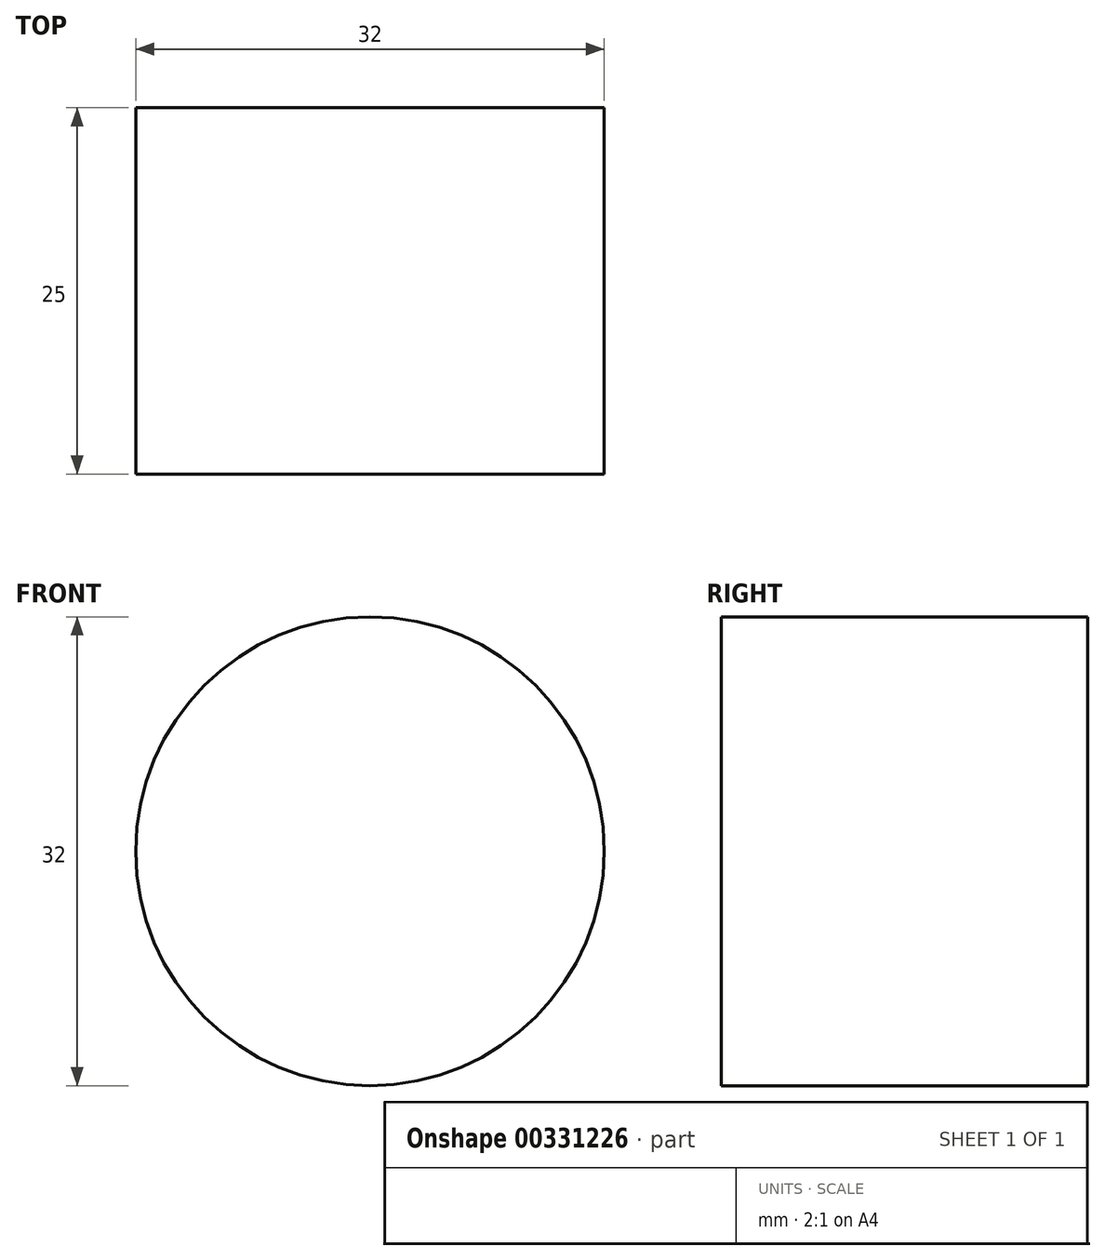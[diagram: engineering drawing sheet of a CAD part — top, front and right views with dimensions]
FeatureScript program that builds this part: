
annotation { "Feature Type Name" : "Feature", "Feature Type Description" : "" }
export const myFeature = defineFeature(function(context is Context, id is Id, definition is map)
    precondition{}
    {
        {
            var Q0;
            Q0=qCreatedBy(makeId("Front.planeOp"),FACE);
            var sketch = newSketch(context, id + "F0", { "sketchPlane" : qUnion([Q0])});
            skLineSegment(sketch, "E0", {"start": v(-190.5, 15.32) * mm, "end": v(191.35, 15.32) * mm});
            skSolve(sketch);
        }
        {
            var Q0;
            Q0=qCreatedBy(makeId("Front.planeOp"),FACE);
            var sketch = newSketch(context, id + "F1", { "sketchPlane" : qUnion([Q0])});
            skCircle(sketch, "E1", {"center": v(0, 45.45) * mm, "radius": 30 * mm});
            skSolve(sketch);
        }
        {
            var Q0;
            Q0=makeQuery(id+"F1.imprint","IMPRINT",FACE,{"disambiguationData":[TD([[makeQuery(id+"F1.imprint","IMPRINT",EDGE,{"derivedFrom":sQuery(id+"F1.wireOp",EDGE,"E1")}),1.0]])]});
            var sketch = newSketch(context, id + "F2", { "sketchPlane" : qUnion([Q0])});
            skCircle(sketch, "E2", {"center": v(0, 45) * mm, "radius": 16 * mm});
            skSolve(sketch);
        }
        {
            var Q0;
            Q0=makeQuery(id+"F2.imprint","IMPRINT",FACE,{"disambiguationData":[TD([[makeQuery(id+"F2.imprint","IMPRINT",EDGE,{"derivedFrom":sQuery(id+"F2.wireOp",EDGE,"E2")}),1.0]])]});
            extrude(context, id + "F3", {"entities" : qUnion([Q0]), "depth" : 25 * mm});
        }
        {
            var Q0;
            Q0=sQuery(id+"F0.wireOp",EDGE,"E0");
            extrude(context, id + "F4", {"bodyType" : ToolBodyType.SURFACE, "operationType" : NewBodyOperationType.INTERSECT, "surfaceEntities" : qUnion([Q0]), "oppositeDirection" : true, "depth" : 25 * mm});
        }
    });
